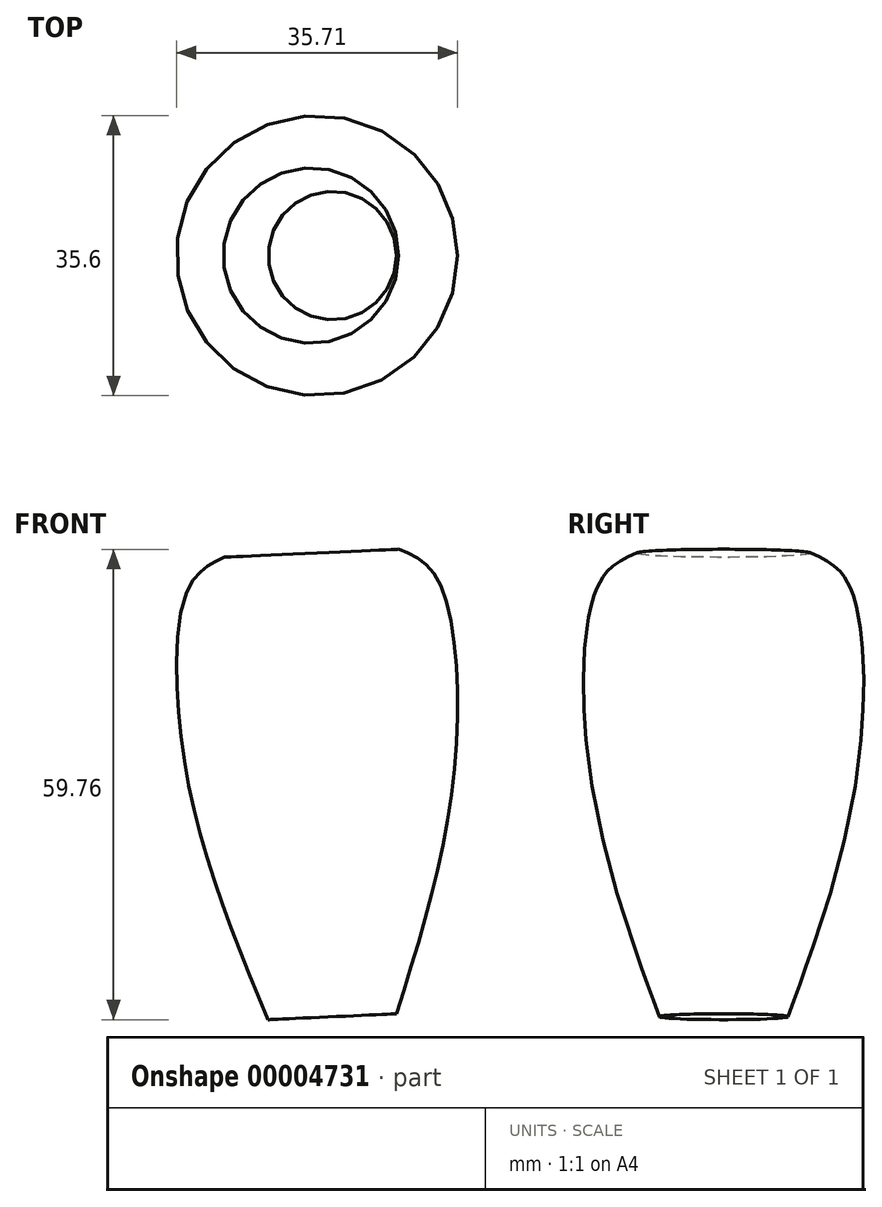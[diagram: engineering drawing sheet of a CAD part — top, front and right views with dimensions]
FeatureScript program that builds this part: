
annotation { "Feature Type Name" : "Feature", "Feature Type Description" : "" }
export const myFeature = defineFeature(function(context is Context, id is Id, definition is map)
    precondition{}
    {
        {
            var Q0;
            Q0=qCreatedBy(makeId("Front.planeOp"),FACE);
            var sketch = newSketch(context, id + "F0", { "sketchPlane" : qUnion([Q0])});
            skFitSpline(sketch, "E0", {"points": [v(-8.16, 0) * mm, v(-18.3, 30.05) * mm, v(-18.3, 54.78) * mm, v(-13.85, 58.74) * mm], "startDerivative": vector(-27.96, 66.75) * mm, "endDerivative": vector(27.06, 13.54) * mm});
            skLineSegment(sketch, "E1", {"start": v(0, 0) * mm, "end": v(-3.22, 69.87) * mm});
            skSolve(sketch);
        }
        {
            var Q0;
            Q0=sQuery(id+"F0.wireOp",EDGE,"E0");
            var Q1;
            Q1=sQuery(id+"F0.wireOp",EDGE,"E1");
            revolve(context, id + "F1", {"bodyType" : ToolBodyType.SURFACE, "surfaceEntities" : qUnion([Q0]), "axis" : qUnion([Q1]), "revolveType" : RevolveType.FULL});
        }
    });
